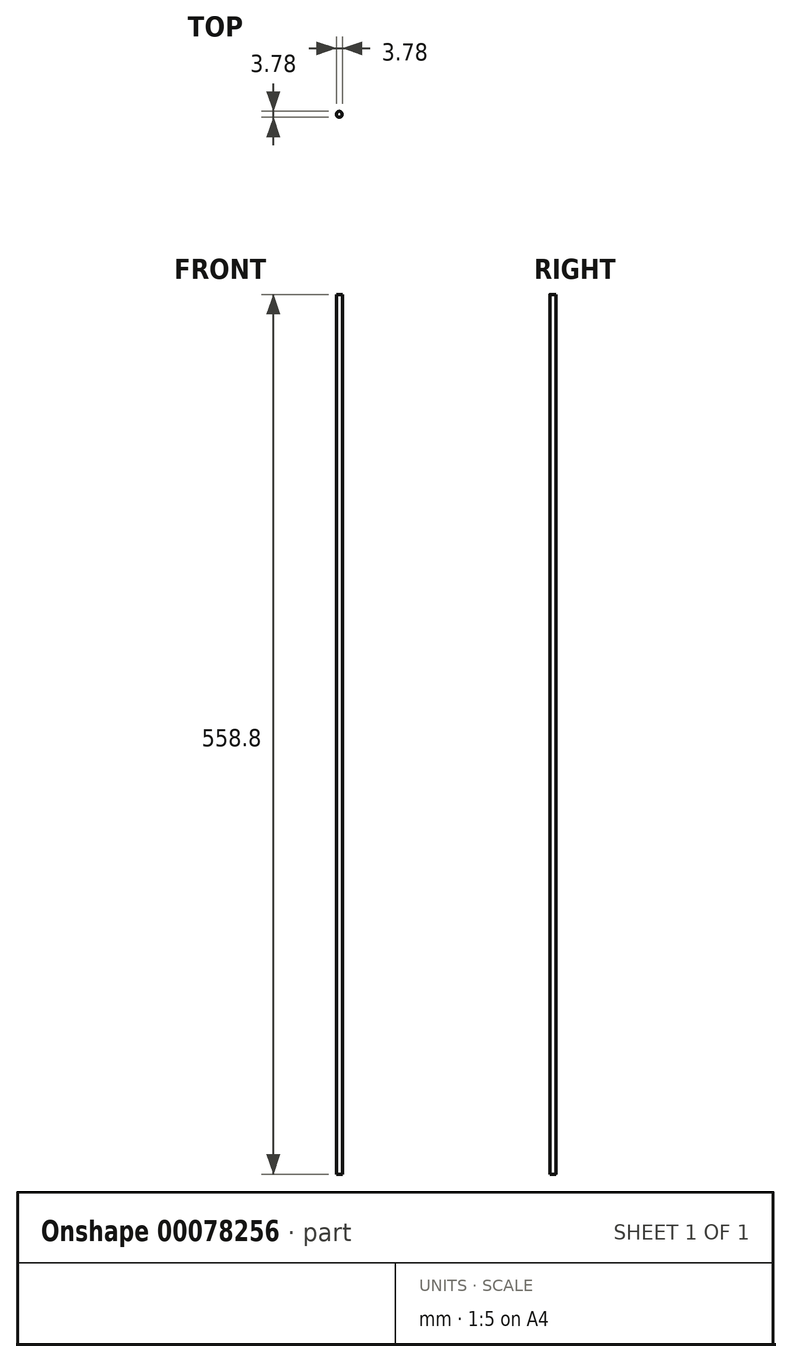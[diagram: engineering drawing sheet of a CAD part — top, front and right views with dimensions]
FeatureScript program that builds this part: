
annotation { "Feature Type Name" : "Feature", "Feature Type Description" : "" }
export const myFeature = defineFeature(function(context is Context, id is Id, definition is map)
    precondition{}
    {
        {
            var Q0;
            Q0=qCreatedBy(makeId("Top.planeOp"),FACE);
            var sketch = newSketch(context, id + "F0", { "sketchPlane" : qUnion([Q0])});
            skCircle(sketch, "E0", {"center": v(0, 0) * mm, "radius": 1.9 * mm});
            skSolve(sketch);
        }
        {
            var Q0;
            Q0=makeQuery(id+"F0.imprint","IMPRINT",FACE,{"disambiguationData":[TD([[makeQuery(id+"F0.imprint","IMPRINT",EDGE,{"derivedFrom":sQuery(id+"F0.wireOp",EDGE,"E0")}),1.0]])]});
            extrude(context, id + "F1", {"entities" : qUnion([Q0]), "depth" : 558.8 * mm});
        }
    });
